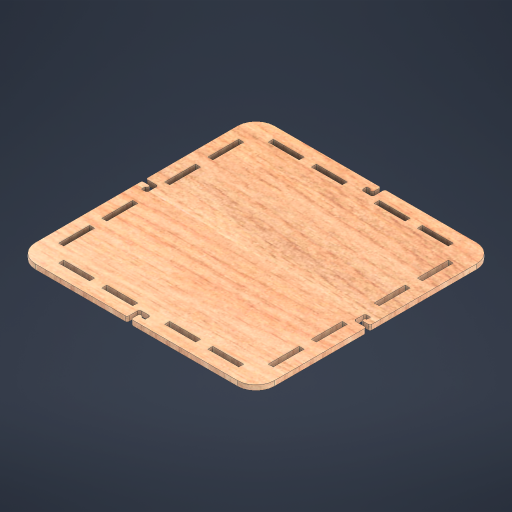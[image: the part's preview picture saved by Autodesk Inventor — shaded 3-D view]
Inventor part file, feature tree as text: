
AUTODESK INVENTOR PART (.ipt)
format: ipt  version: 2024.1 (Build 281209000, 209)  size: 510,464 bytes
history: native  units: mm
features: extrude x1, fillet x1, sketch x1
ambient origin geometry x8: Origin, YZ Plane, XZ Plane, XY Plane, X Axis, Y Axis, Z Axis, Center Point
bodies: Solid1 (feature_tree)
feature tree (3):
  extrude  "Extrusion1"  Depth=4.0mm
  fillet  "Fillet1"  Radius=10.0mm
  sketch  "Sketch1"  dims[d0=25.0mm d1=4.0mm d4=10.0mm d5=13.0mm d6=10.0mm d7=10.0mm d8=10.0mm d9=13.0mm d10=40.0mm d12=360.0deg d14=10.0mm d15=10.0mm d16=15.0mm d17=7.0mm d18=3.0mm d19=6.0mm d20=3.0mm d21=1.5mm d22=40.0mm d24=360.0deg d26=4.0mm d27=0.0mm d28=1.5mm]
